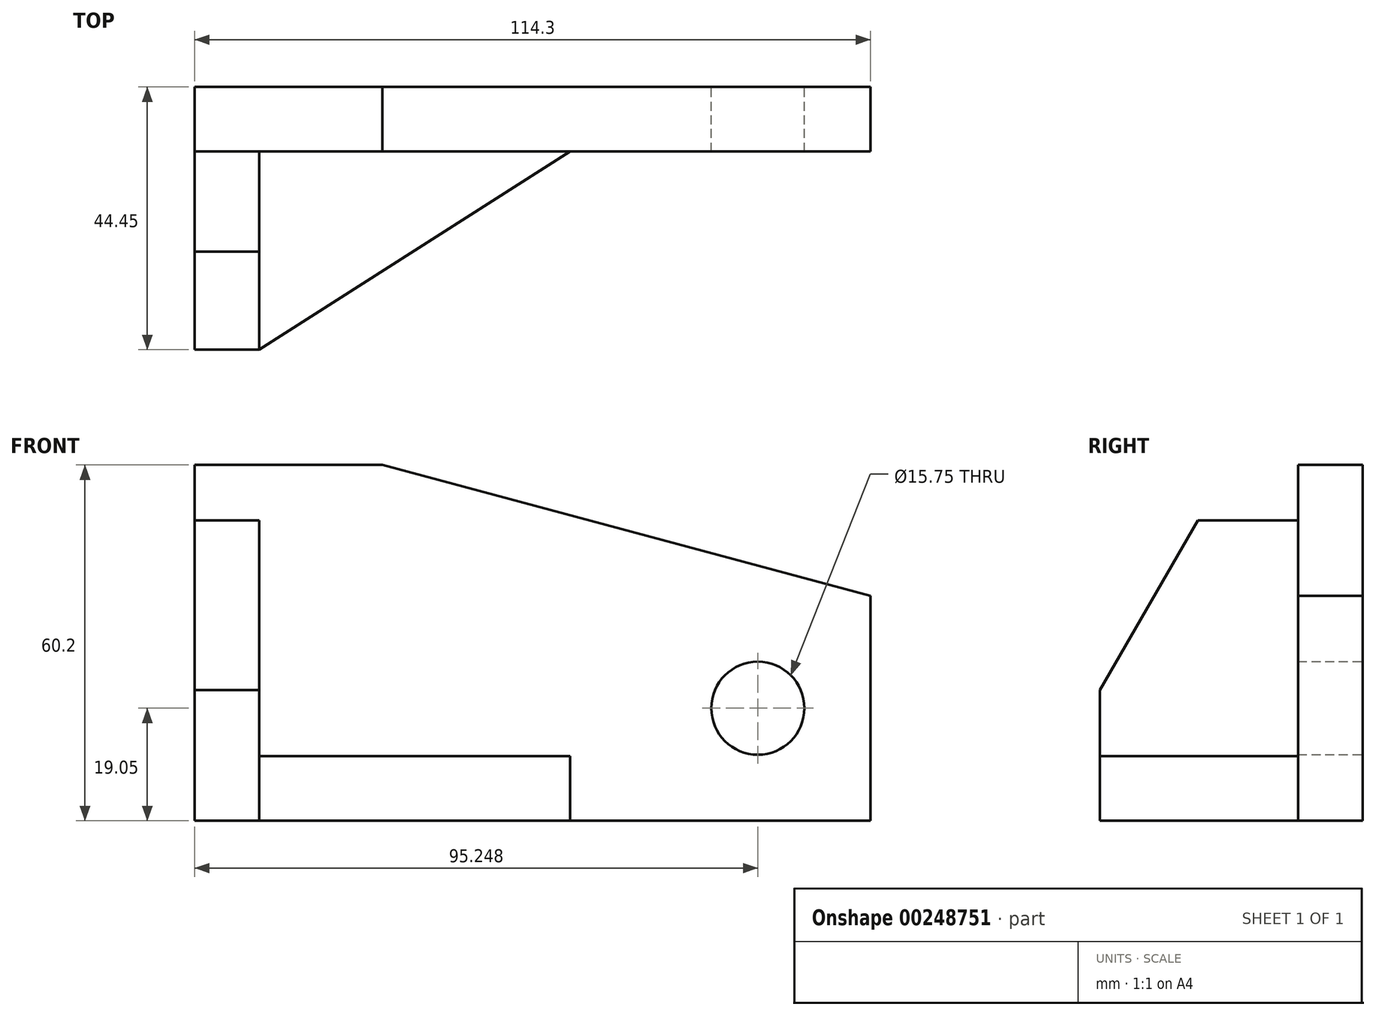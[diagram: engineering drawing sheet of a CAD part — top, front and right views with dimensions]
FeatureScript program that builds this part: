
annotation { "Feature Type Name" : "Feature", "Feature Type Description" : "" }
export const myFeature = defineFeature(function(context is Context, id is Id, definition is map)
    precondition{}
    {
        {
            var Q0;
            Q0=qCreatedBy(makeId("Front.planeOp"),FACE);
            var sketch = newSketch(context, id + "F0", { "sketchPlane" : qUnion([Q0])});
            skLineSegment(sketch, "E0", {"start": v(-49.44, 41.15) * mm, "end": v(-17.7, 41.15) * mm});
            skLineSegment(sketch, "E1", {"start": v(-49.44, 41.15) * mm, "end": v(-49.44, -19.05) * mm});
            skLineSegment(sketch, "E2", {"start": v(-49.44, -19.05) * mm, "end": v(64.86, -19.05) * mm});
            skLineSegment(sketch, "E3", {"start": v(64.86, -19.05) * mm, "end": v(64.86, 19.03) * mm});
            skLineSegment(sketch, "E4", {"start": v(64.86, 19.03) * mm, "end": v(-17.7, 41.15) * mm});
            skLineSegment(sketch, "E5.bottom", {"start": v(-38.52, -8.13) * mm, "end": v(14.06, -8.13) * mm});
            skLineSegment(sketch, "E5.right", {"start": v(14.06, -8.13) * mm, "end": v(14.06, -19.05) * mm});
            skCircle(sketch, "E6", {"center": v(45.8, 0) * mm, "radius": 7.87 * mm});
            skLineSegment(sketch, "E7", {"start": v(-49.44, 31.75) * mm, "end": v(-38.52, 31.75) * mm});
            skLineSegment(sketch, "E8", {"start": v(-38.52, 31.75) * mm, "end": v(-38.52, -8.13) * mm});
            skSolve(sketch);
        }
        {
            var Q0;
            Q0=makeQuery(id+"F0.imprint","IMPRINT",FACE,{"disambiguationData":[TD([[makeQuery(id+"F0.imprint","IMPRINT",EDGE,{"derivedFrom":sQuery(id+"F0.wireOp",EDGE,"E5.bottom")}),-1.0]])]});
            extrude(context, id + "F1", {"entities" : qUnion([Q0]), "depth" : 44.45 * mm});
        }
        {
            var Q0;
            Q0=makeQuery(id+"F0.imprint","IMPRINT",FACE,{"disambiguationData":[TD([[makeQuery(id+"F0.imprint","IMPRINT",EDGE,{"derivedFrom":sQuery(id+"F0.wireOp",EDGE,"E0")}),-1.0]])]});
            extrude(context, id + "F2", {"entities" : qUnion([Q0]), "operationType" : NewBodyOperationType.ADD, "depth" : 10.92 * mm});
        }
        {
            var Q0;
            Q0=makeQuery(id+"F1.opExtrude","SWEPT_FACE",FACE,{"disambiguationData":[OSD([sQuery(id+"F0.wireOp",EDGE,"E5.bottom")])]});
            var sketch = newSketch(context, id + "F3", { "sketchPlane" : qUnion([Q0])});
            skLineSegment(sketch, "E9", {"start": v(-38.52, -44.45) * mm, "end": v(14.06, -10.92) * mm});
            skSolve(sketch);
        }
        {
            var Q0;
            Q0 = qSketchRegion(id + "F3", true);
            var Q1;
            Q1=makeQuery(id+"F3.imprint","IMPRINT",FACE,{"disambiguationData":[TD([[makeQuery(id+"F3.imprint","IMPRINT",EDGE,{"derivedFrom":sQuery(id+"F3.wireOp",EDGE,"E9")}),-1.0]])]});
            extrude(context, id + "F4", {"entities" : qUnion([Q0, Q1]), "operationType" : NewBodyOperationType.REMOVE, "oppositeDirection" : true, "depth" : 25.4 * mm});
        }
        {
            var Q0;
            Q0=makeQuery(id+"F1.opExtrude","SWEPT_FACE",FACE,{"disambiguationData":[OSD([sQuery(id+"F0.wireOp",EDGE,"E8")])]});
            var sketch = newSketch(context, id + "F5", { "sketchPlane" : qUnion([Q0])});
            skLineSegment(sketch, "E10", {"start": v(-27.88, 31.75) * mm, "end": v(-44.45, 3.05) * mm});
            skSolve(sketch);
        }
        {
            var Q0;
            {var subQ0=sQuery(id+"F5.wireOp",EDGE,"E10");Q0=makeQuery(id+"F5.imprint","IMPRINT",FACE,{"disambiguationData":[TD([[makeQuery(id+"F5.imprint","IMPRINT",EDGE,{"derivedFrom":subQ0}),-1.0]])]});}
            extrude(context, id + "F6", {"entities" : qUnion([Q0]), "operationType" : NewBodyOperationType.REMOVE, "oppositeDirection" : true, "depth" : 25.4 * mm});
        }
    });
